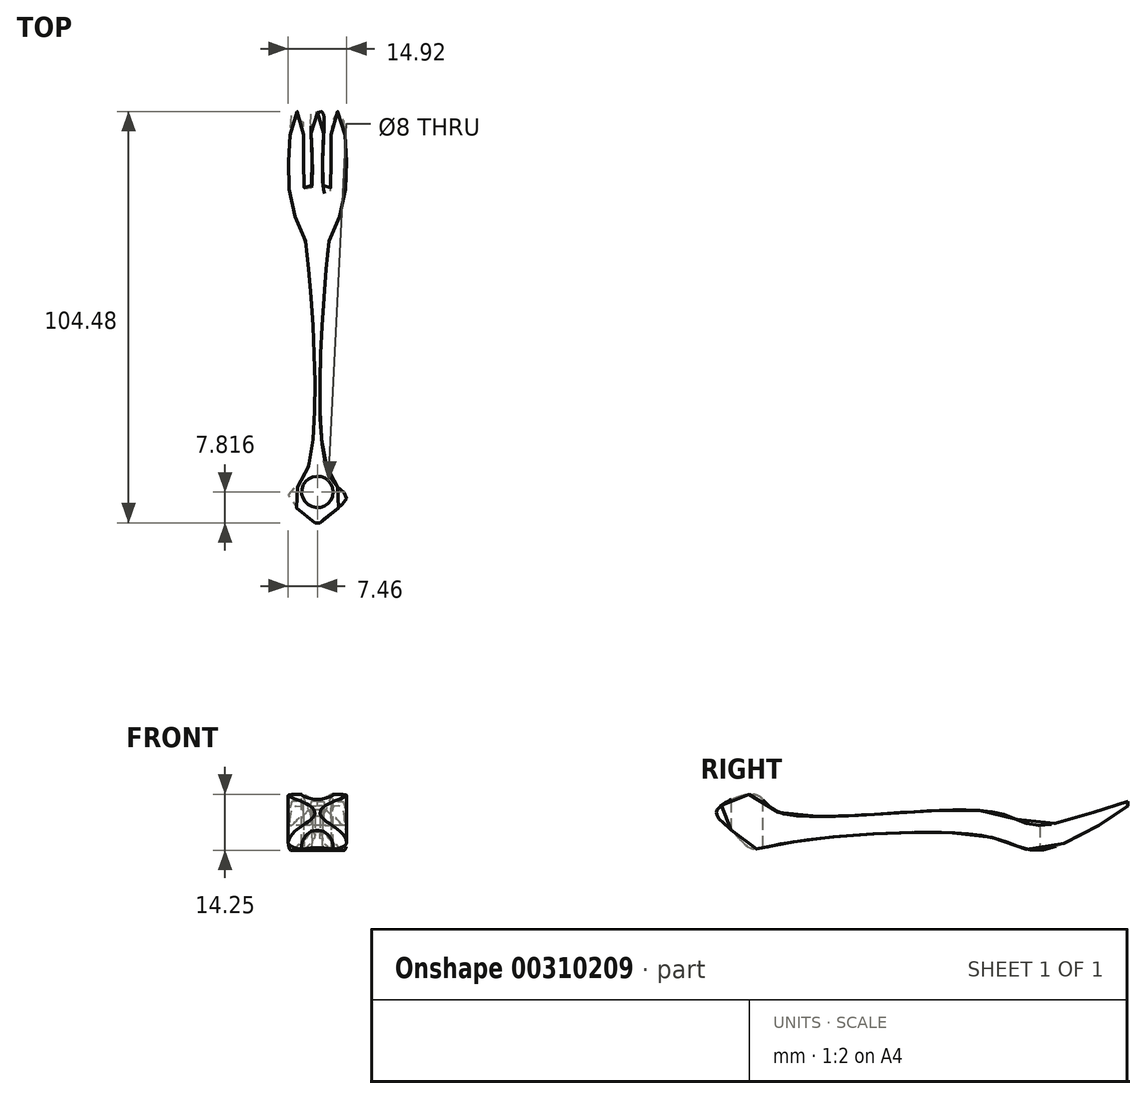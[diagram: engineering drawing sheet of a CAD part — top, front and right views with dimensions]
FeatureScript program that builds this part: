
annotation { "Feature Type Name" : "Feature", "Feature Type Description" : "" }
export const myFeature = defineFeature(function(context is Context, id is Id, definition is map)
    precondition{}
    {
        {
            var Q0;
            Q0=qCreatedBy(makeId("Top.planeOp"),FACE);
            var sketch = newSketch(context, id + "F0", { "sketchPlane" : qUnion([Q0])});
            skLineSegment(sketch, "E0.bottom", {"start": v(-14.9, 62.67) * mm, "end": v(15.1, 62.67) * mm});
            skLineSegment(sketch, "E0.top", {"start": v(-14.9, -47.33) * mm, "end": v(15.1, -47.33) * mm});
            skLineSegment(sketch, "E0.left", {"start": v(-14.9, 62.67) * mm, "end": v(-14.9, -47.33) * mm});
            skLineSegment(sketch, "E0.right", {"start": v(15.1, 62.67) * mm, "end": v(15.1, -47.33) * mm});
            skPoint(sketch, "E0.middle", {"position": v(0.1, 7.67) * mm});
            skSolve(sketch);
        }
        {
            var Q0;
            Q0=makeQuery(id+"F0.imprint","IMPRINT",FACE,{"disambiguationData":[TD([[makeQuery(id+"F0.imprint","IMPRINT",EDGE,{"derivedFrom":sQuery(id+"F0.wireOp",EDGE,"E0.bottom")}),-1.0]])]});
            extrude(context, id + "F1", {"entities" : qUnion([Q0]), "depth" : 30 * mm});
        }
        {
            var Q0;
            Q0=makeQuery(id+"F1.opExtrude","CAP_FACE",FACE,{"disambiguationData":[OSD([sQuery(id+"F0.wireOp",EDGE,"E0.bottom"),sQuery(id+"F0.wireOp",EDGE,"E0.top"),sQuery(id+"F0.wireOp",EDGE,"E0.left"),sQuery(id+"F0.wireOp",EDGE,"E0.right")])],"isStart":false});
            var sketch = newSketch(context, id + "F2", { "sketchPlane" : qUnion([Q0])});
            skFitSpline(sketch, "E1", {"points": [v(0, 61.65) * mm, v(1.07, 61.9) * mm, v(1.62, 60.94) * mm, v(1.62, 41.76) * mm, v(2.9, 39.78) * mm, v(3.84, 60.94) * mm, v(4.8, 61.9) * mm, v(6.14, 61.65) * mm, v(6.7, 59.51) * mm, v(6.85, 39.78) * mm, v(3.2, 29.64) * mm, v(2.36, 24.07) * mm, v(3.14, -30.7) * mm, v(7.46, -35.95) * mm, v(4.36, -39.63) * mm, v(1.93, -41.45) * mm, v(0, -43.28) * mm], "startDerivative": vector(46.75, 16.44) * mm, "endDerivative": vector(-39.36, -50.54) * mm});
            skFitSpline(sketch, "E2.MirrorCS", {"points": [v(0, 61.65) * mm, v(-1.07, 61.9) * mm, v(-1.62, 60.94) * mm, v(-1.62, 41.76) * mm, v(-2.9, 39.78) * mm, v(-3.84, 60.94) * mm, v(-4.8, 61.9) * mm, v(-6.14, 61.65) * mm, v(-6.7, 59.51) * mm, v(-6.85, 39.78) * mm, v(-3.2, 29.64) * mm, v(-2.36, 24.07) * mm, v(-3.14, -30.7) * mm, v(-7.46, -35.95) * mm, v(-4.36, -39.63) * mm, v(-1.93, -41.45) * mm, v(0, -43.28) * mm], "startDerivative": vector(-46.75, 16.44) * mm, "endDerivative": vector(39.36, -50.54) * mm});
            skSolve(sketch);
        }
        {
            var Q0;
            Q0=makeQuery(id+"F1.opExtrude","SWEPT_FACE",FACE,{"disambiguationData":[OSD([sQuery(id+"F0.wireOp",EDGE,"E0.right")])]});
            var sketch = newSketch(context, id + "F3", { "sketchPlane" : qUnion([Q0])});
            skFitSpline(sketch, "E3", {"points": [v(62.67, 24.42) * mm, v(40.84, 18.4) * mm, v(27.26, 21.84) * mm, v(-27.26, 21.84) * mm, v(-32.74, 26.14) * mm, v(-42.47, 22.12) * mm, v(-39.22, 17.54) * mm, v(-34.16, 12.66) * mm, v(-26.86, 13.52) * mm, v(27.47, 15.24) * mm, v(41.66, 12.38) * mm, v(62.67, 24.42) * mm]});
            skSolve(sketch);
        }
        {
            var Q0;
            {var subQ0=sQuery(id+"F0.wireOp",EDGE,"E0.right");var subQ2=makeQuery(id+"F1.opExtrude","CAP_EDGE",EDGE,{"disambiguationData":[OSD([subQ0])],"isStart":true});Q0=makeQuery(id+"F3.imprint","IMPRINT",FACE,{"disambiguationData":[TD([[makeQuery(id+"F3.imprint","IMPRINT",EDGE,{"derivedFrom":subQ2}),-1.0]])]});}
            extrude(context, id + "F4", {"entities" : qUnion([Q0]), "operationType" : NewBodyOperationType.REMOVE, "oppositeDirection" : true, "depth" : 30 * mm});
        }
        {
            var Q0;
            Q0=makeQuery(id+"F2.imprint","IMPRINT",FACE,{"disambiguationData":[TD([[makeQuery(id+"F2.imprint","IMPRINT",EDGE,{"derivedFrom":sQuery(id+"F2.wireOp",EDGE,"E1")}),1.0]])]});
            extrude(context, id + "F5", {"entities" : qUnion([Q0]), "operationType" : NewBodyOperationType.REMOVE, "oppositeDirection" : true, "depth" : 30 * mm});
        }
        {
            var Q0;
            Q0=qCreatedBy(makeId("Top.planeOp"),FACE);
            var sketch = newSketch(context, id + "F6", { "sketchPlane" : qUnion([Q0])});
            skCircle(sketch, "E4", {"center": v(0, -34.76) * mm, "radius": 4 * mm});
            skSolve(sketch);
        }
        {
            var Q0;
            Q0 = qSketchRegion(id + "F6", true);
            extrude(context, id + "F7", {"entities" : qUnion([Q0]), "operationType" : NewBodyOperationType.REMOVE, "endBound" : BoundingType.SYMMETRIC, "oppositeDirection" : true, "depth" : 60 * mm});
        }
    });
